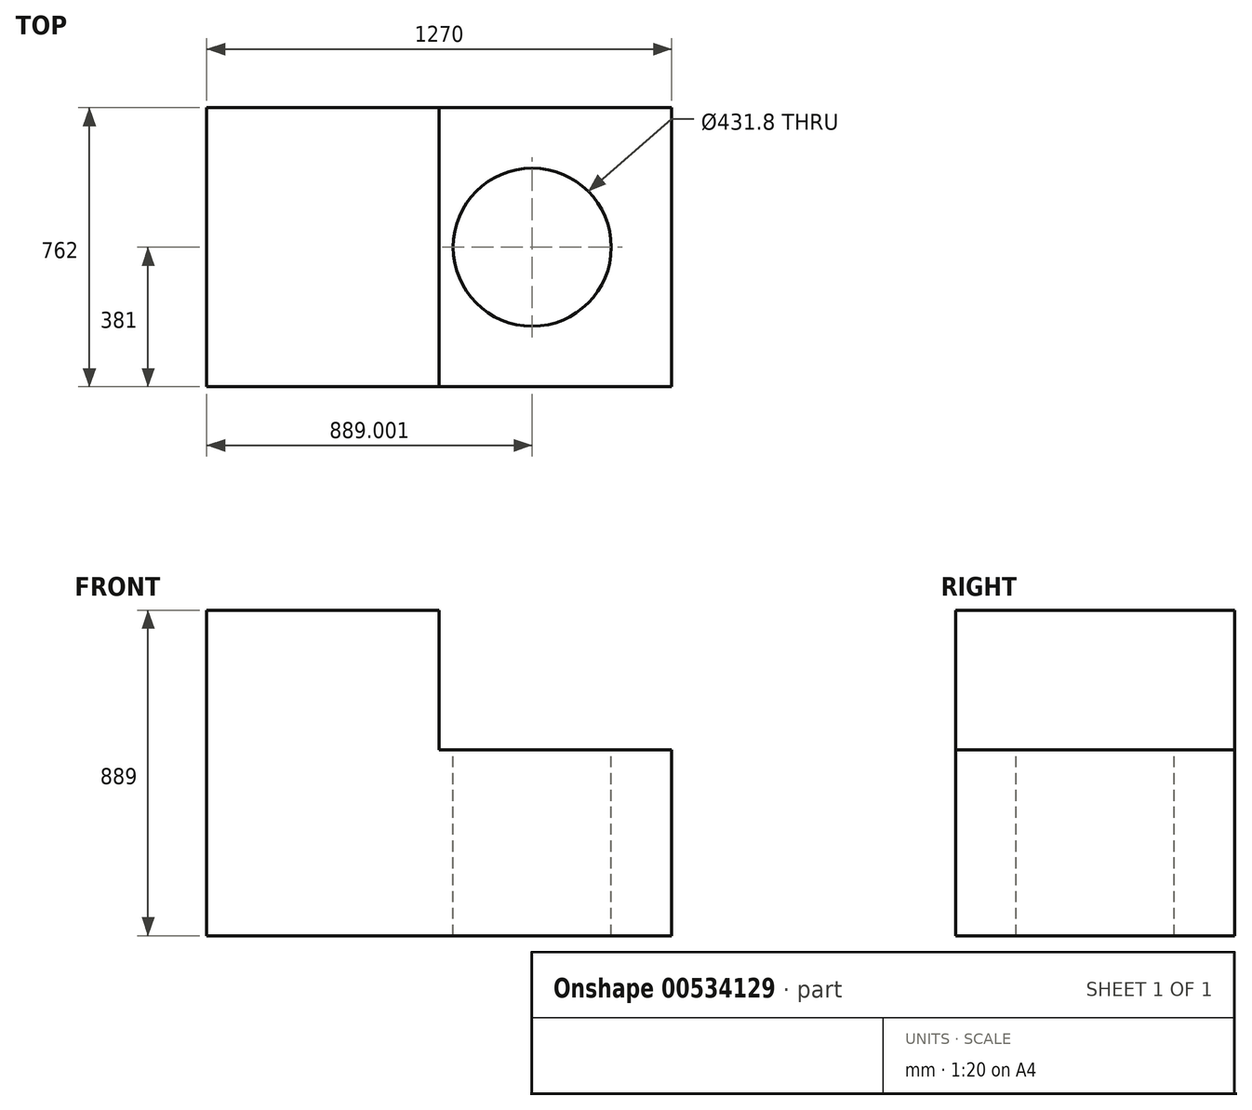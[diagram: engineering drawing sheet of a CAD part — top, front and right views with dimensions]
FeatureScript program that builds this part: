
annotation { "Feature Type Name" : "Feature", "Feature Type Description" : "" }
export const myFeature = defineFeature(function(context is Context, id is Id, definition is map)
    precondition{}
    {
        {
            var Q0;
            Q0=qCreatedBy(makeId("Front.planeOp"),FACE);
            var sketch = newSketch(context, id + "F0", { "sketchPlane" : qUnion([Q0])});
            skLineSegment(sketch, "E0.bottom", {"start": v(-628.14, 502.26) * mm, "end": v(6.86, 502.26) * mm});
            skLineSegment(sketch, "E0.top", {"start": v(-628.14, -386.74) * mm, "end": v(641.86, -386.74) * mm});
            skLineSegment(sketch, "E0.left", {"start": v(-628.14, 502.26) * mm, "end": v(-628.14, -386.74) * mm});
            skLineSegment(sketch, "E0.right", {"start": v(641.86, 121.26) * mm, "end": v(641.86, -386.74) * mm});
            skLineSegment(sketch, "E1", {"start": v(6.86, 502.26) * mm, "end": v(6.86, 121.26) * mm});
            skLineSegment(sketch, "E2", {"start": v(6.86, 121.26) * mm, "end": v(641.86, 121.26) * mm});
            skSolve(sketch);
        }
        {
            var Q0;
            Q0=makeQuery(id+"F0.imprint","IMPRINT",FACE,{"disambiguationData":[TD([[makeQuery(id+"F0.imprint","IMPRINT",EDGE,{"derivedFrom":sQuery(id+"F0.wireOp",EDGE,"E0.bottom")}),-1.0]])]});
            extrude(context, id + "F1", {"entities" : qUnion([Q0]), "depth" : 762 * mm, "offsetDistance" : 25.4 * mm});
        }
        {
            var Q0;
            Q0=makeQuery(id+"F1.opExtrude","SWEPT_FACE",FACE,{"disambiguationData":[OSD([sQuery(id+"F0.wireOp",EDGE,"E2")])]});
            var sketch = newSketch(context, id + "F2", { "sketchPlane" : qUnion([Q0])});
            skPoint(sketch, "E3.startSnap0", {"position": v(6.86, -381) * mm});
            skCircle(sketch, "E4", {"center": v(260.86, -381) * mm, "radius": 215.9 * mm});
            skSolve(sketch);
        }
        {
            var Q0;
            Q0=makeQuery(id+"F2.imprint","IMPRINT",FACE,{"disambiguationData":[TD([[makeQuery(id+"F2.imprint","IMPRINT",EDGE,{"derivedFrom":sQuery(id+"F2.wireOp",EDGE,"E4")}),1.0]])]});
            extrude(context, id + "F3", {"entities" : qUnion([Q0]), "operationType" : NewBodyOperationType.REMOVE, "oppositeDirection" : true, "depth" : 508 * mm, "offsetDistance" : 25.4 * mm});
        }
    });
